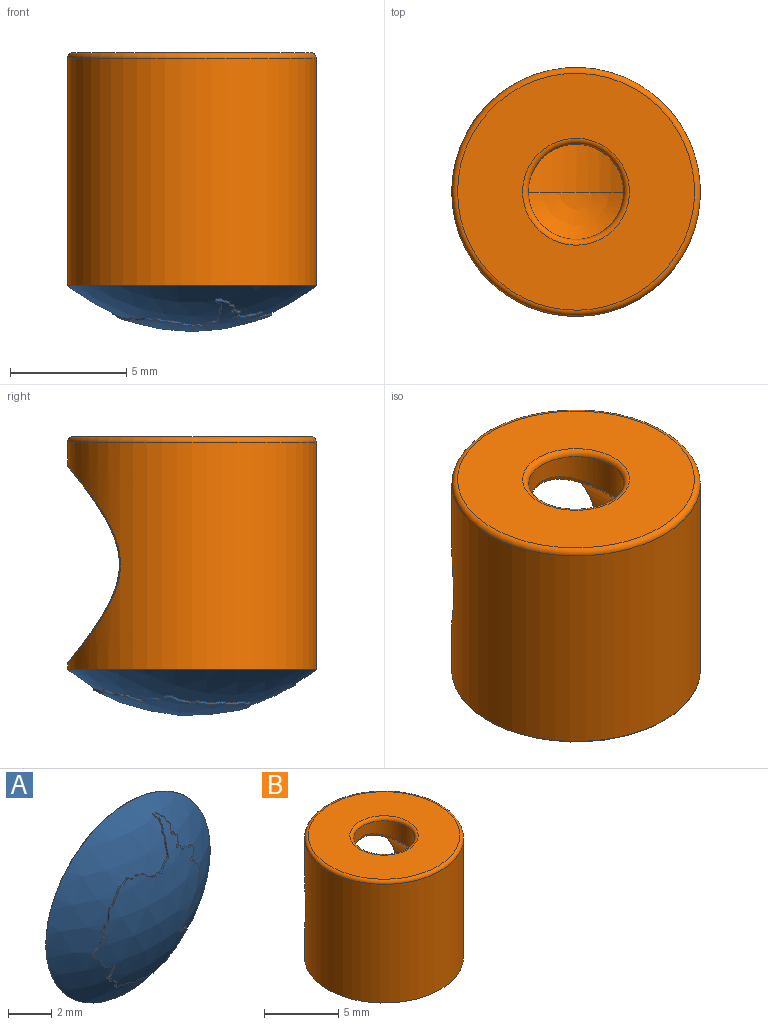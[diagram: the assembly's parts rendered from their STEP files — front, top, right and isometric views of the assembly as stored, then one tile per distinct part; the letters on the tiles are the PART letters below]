
ASSEMBLY  parts=2 mates=1
PART A: 6 faces, bbox 10.7x3.5x10.8 mm
  f0: sphere r=8.59mm, area 28.1mm2, adj f1,f2
  f1: extruded ~8.69x3.8mm, area 1.3mm2, adj f0,f2,f3
  f2: extruded ~8.46x4.63mm, area 0.8mm2, adj f0,f1,f3
  f3: sphere r=8.51mm, area 74.3mm2, adj f1,f2,f4
  f4: cylinder r=5.35mm len=10.7mm, axis (0,1,0), area 0.6mm2, adj f3,f5
  f5: plane 10.7x10.7mm, normal (0,1,0), area 89.9mm2, adj f4
PART B: 11 faces, bbox 11.6x11.6x10 mm
  f0: sphere r=4.15mm, area 100.2mm2, adj f3,f6
  f1: cylinder r=2.05mm len=4.1mm, axis (0,0,-1), area 17.3mm2, adj f6,f7,f8
  f2: cylinder r=5.35mm len=10.7mm, axis (0,0,-1), area 263mm2, adj f4,f9,f10
  f3: cylinder r=4.15mm len=8.3mm, axis (0,-1,0), area 101.1mm2, adj f0,f4,f7
  f4: bspline ~8.76x8.56mm, area 7.1mm2, adj f2,f3
  f5: plane 10.2x10.2mm, normal (0,0,1), area 65.1mm2, adj f8,f9
  f6: torus R=2.3mm, axis (0,0,-1), area 1.7mm2, adj f0,f1,f7
  f7: bspline ~4.34x2.42mm, area 2.2mm2, adj f1,f3,f6
  f8: torus R=2.3mm, axis (0,0,-1), area 5.3mm2, adj f1,f5
  f9: torus R=5.1mm, axis (0,0,-1), area 13mm2, adj f2,f5
  f10: plane 10.7x10.7mm, normal (0,0,-1), area 89.9mm2, adj f2
PLACE A rot(axis=(1,0,0),90deg) t=(0,0,1.71)mm
PLACE B t=(0,0,1.39)mm
MATE fastened A.f4 <-> B.f1  axis (0,0,1) through (0,0,-4.89)mm
